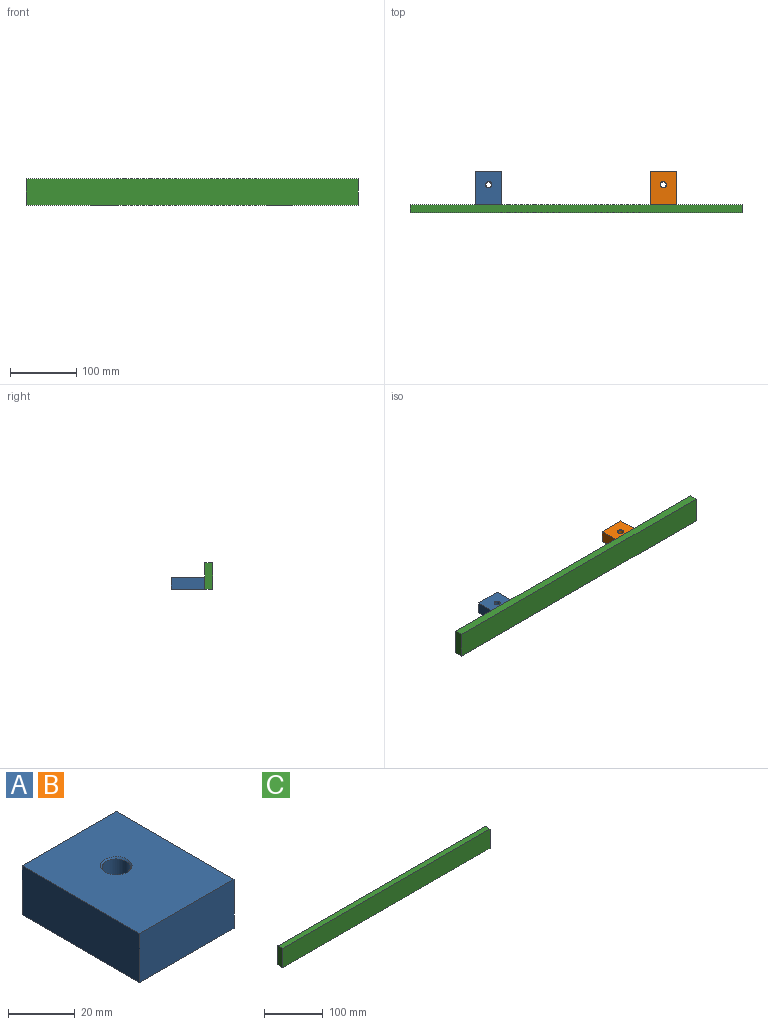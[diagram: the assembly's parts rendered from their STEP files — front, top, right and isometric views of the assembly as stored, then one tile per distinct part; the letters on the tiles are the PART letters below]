
ASSEMBLY  parts=3 mates=2
PART A: 8 faces, bbox 40x50x18 mm
  f0: plane 50x18mm, normal (1,0,0), area 900mm2, adj f1,f3,f4,f5
  f1: plane 50x40mm, normal (0,0,1), area 1929.1mm2, adj f0,f2,f4,f5,f7
  f2: plane 50x18mm, normal (-1,0,0), area 900mm2, adj f1,f3,f4,f5
  f3: plane 50x40mm, normal (0,0,-1), area 1943.3mm2, adj f0,f2,f4,f5,f6
  f4: plane 40x18mm, normal (0,1,0), area 720mm2, adj f0,f1,f2,f3
  f5: plane 40x18mm, normal (0,-1,0), area 720mm2, adj f0,f1,f2,f3
  f6: cylinder r=4.25mm len=17.5mm, axis (0,0,1), area 467.3mm2, adj f3,f7
  f7: cone r=4.25mm half-angle=45deg, axis (0,0,1), area 20mm2, adj f1,f6
PART B: same geometry as A
PART C: 6 faces, bbox 500x12x40 mm
  f0: plane 40x12mm, normal (1,0,0), area 480mm2, adj f1,f3,f4,f5
  f1: plane 500x40mm, normal (0,1,0), area 20000mm2, adj f0,f2,f4,f5
  f2: plane 40x12mm, normal (-1,0,0), area 480mm2, adj f1,f3,f4,f5
  f3: plane 500x40mm, normal (0,-1,0), area 20000mm2, adj f0,f2,f4,f5
  f4: plane 500x12mm, normal (0,0,1), area 6000mm2, adj f0,f1,f2,f3
  f5: plane 500x12mm, normal (0,0,-1), area 6000mm2, adj f0,f1,f2,f3
PLACE A t=(-131.5,6,9)mm
PLACE B t=(131.5,6,9)mm
PLACE C at identity fixed
MATE fastened A.f5 <-> C.f1  axis (0,-1,0) through (-151.5,6,0)mm
MATE fastened B.f5 <-> C.f1  axis (0,-1,0) through (151.5,6,0)mm
